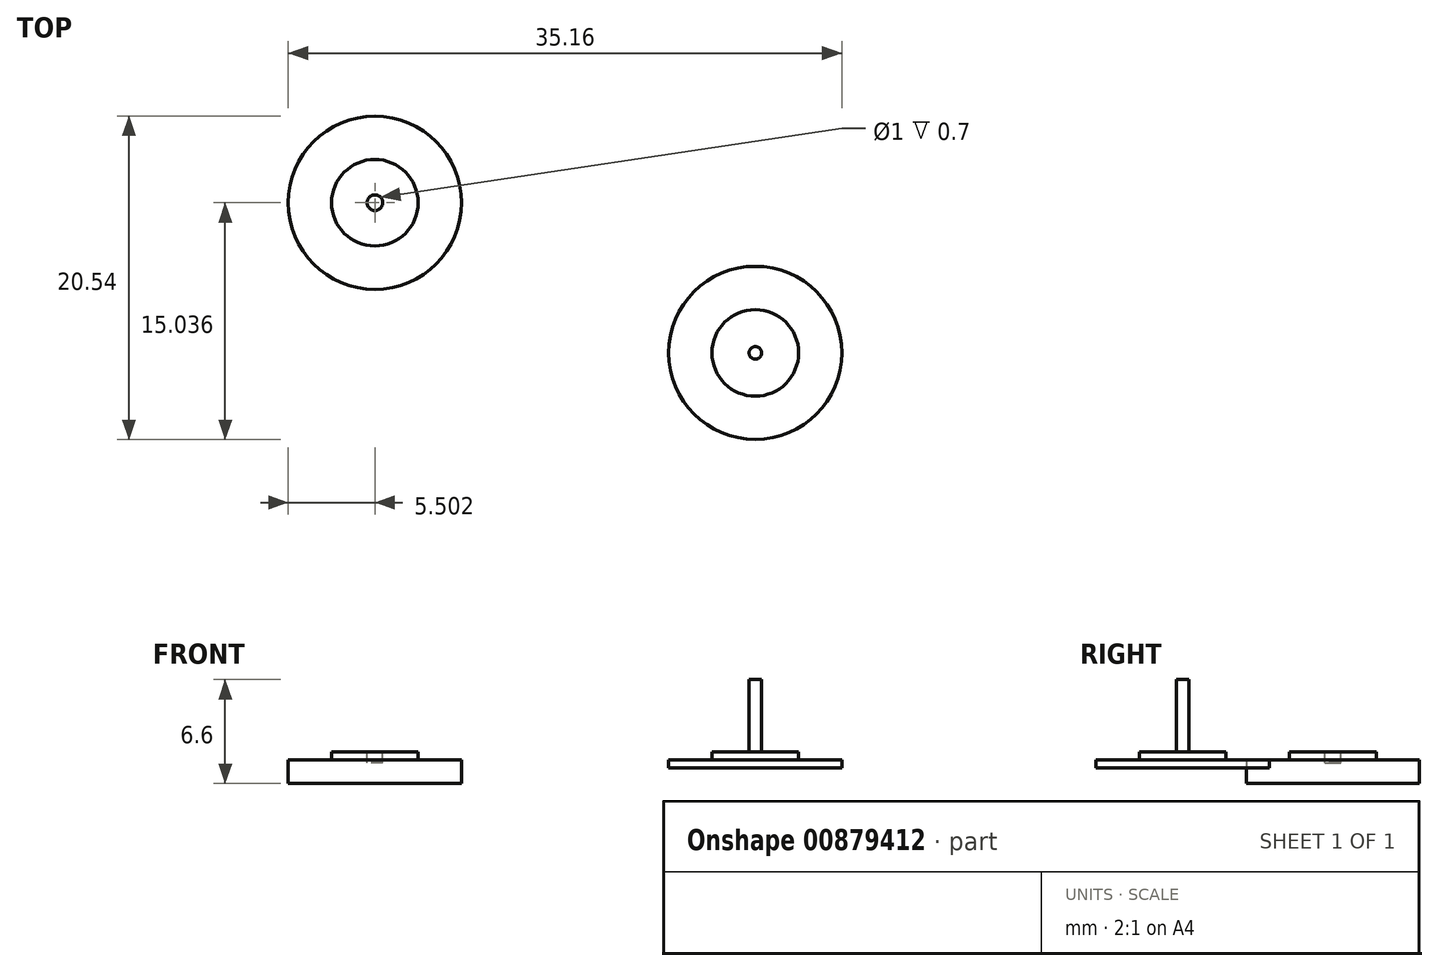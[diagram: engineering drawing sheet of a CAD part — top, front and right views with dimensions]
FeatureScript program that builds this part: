
annotation { "Feature Type Name" : "Feature", "Feature Type Description" : "" }
export const myFeature = defineFeature(function(context is Context, id is Id, definition is map)
    precondition{}
    {
        {
            var Q0;
            Q0=qCreatedBy(makeId("Top.planeOp"),FACE);
            var sketch = newSketch(context, id + "F0", { "sketchPlane" : qUnion([Q0])});
            skCircle(sketch, "E0", {"center": v(-49.28, 41.97) * mm, "radius": 5.5 * mm});
            skSolve(sketch);
        }
        {
            var Q0;
            Q0=makeQuery(id+"F0.imprint","IMPRINT",FACE,{"disambiguationData":[TD([[makeQuery(id+"F0.imprint","IMPRINT",EDGE,{"derivedFrom":sQuery(id+"F0.wireOp",EDGE,"E0")}),1.0]])]});
            extrude(context, id + "F1", {"entities" : qUnion([Q0]), "depth" : .5 * mm, "offsetDistance" : 25.4 * mm});
        }
        {
            var Q0;
            Q0=qCreatedBy(makeId("Top.planeOp"),FACE);
            var sketch = newSketch(context, id + "F2", { "sketchPlane" : qUnion([Q0])});
            skCircle(sketch, "E1", {"center": v(-25.12, 32.43) * mm, "radius": 5.5 * mm});
            skSolve(sketch);
        }
        {
            var Q0;
            Q0=makeQuery(id+"F2.imprint","IMPRINT",FACE,{"disambiguationData":[TD([[makeQuery(id+"F2.imprint","IMPRINT",EDGE,{"derivedFrom":sQuery(id+"F2.wireOp",EDGE,"E1")}),1.0]])]});
            extrude(context, id + "F3", {"entities" : qUnion([Q0]), "depth" : .5 * mm, "offsetDistance" : 25.4 * mm});
        }
        {
            var Q0;
            Q0=qCreatedBy(makeId("Top.planeOp"),FACE);
            var sketch = newSketch(context, id + "F4", { "sketchPlane" : qUnion([Q0])});
            skCircle(sketch, "E2", {"center": v(-49.28, 41.97) * mm, "radius": 2.75 * mm});
            skSolve(sketch);
        }
        {
            var Q0;
            Q0 = qSketchRegion(id + "F4", true);
            extrude(context, id + "F5", {"entities" : qUnion([Q0]), "operationType" : NewBodyOperationType.ADD, "depth" : 1 * mm, "offsetDistance" : 25.4 * mm});
        }
        {
            var Q0;
            Q0=qCreatedBy(makeId("Top.planeOp"),FACE);
            var sketch = newSketch(context, id + "F6", { "sketchPlane" : qUnion([Q0])});
            skCircle(sketch, "E3", {"center": v(-25.12, 32.43) * mm, "radius": 2.75 * mm});
            skSolve(sketch);
        }
        {
            var Q0;
            Q0 = qSketchRegion(id + "F6", true);
            extrude(context, id + "F7", {"entities" : qUnion([Q0]), "operationType" : NewBodyOperationType.ADD, "depth" : 1 * mm, "offsetDistance" : 25.4 * mm});
        }
        {
            var Q0;
            Q0=makeQuery(id+"F5.opExtrude","CAP_FACE",FACE,{"disambiguationData":[OSD([sQuery(id+"F4.wireOp",EDGE,"E2")])],"isStart":false});
            var sketch = newSketch(context, id + "F8", { "sketchPlane" : qUnion([Q0])});
            skCircle(sketch, "E4", {"center": v(-49.28, 41.97) * mm, "radius": 0.5 * mm});
            skSolve(sketch);
        }
        {
            var Q0;
            Q0 = qSketchRegion(id + "F8", true);
            extrude(context, id + "F9", {"entities" : qUnion([Q0]), "operationType" : NewBodyOperationType.REMOVE, "oppositeDirection" : true, "depth" : .7 * mm, "offsetDistance" : 25.4 * mm});
        }
        {
            var Q0;
            Q0=makeQuery(id+"F7.opExtrude","CAP_FACE",FACE,{"disambiguationData":[OSD([sQuery(id+"F6.wireOp",EDGE,"E3")])],"isStart":false});
            var sketch = newSketch(context, id + "F10", { "sketchPlane" : qUnion([Q0])});
            skCircle(sketch, "E5", {"center": v(-25.12, 32.43) * mm, "radius": 0.4 * mm});
            skSolve(sketch);
        }
        {
            var Q0;
            Q0 = qSketchRegion(id + "F10", true);
            extrude(context, id + "F11", {"entities" : qUnion([Q0]), "operationType" : NewBodyOperationType.ADD, "depth" : 4.6 * mm, "offsetDistance" : 25.4 * mm});
        }
        {
            var Q0;
            Q0=sQuery(id+"F2.wireOp",EDGE,"E1");
            extrude(context, id + "F12", {"bodyType" : ToolBodyType.SURFACE, "surfaceEntities" : qUnion([Q0]), "oppositeDirection" : true, "depth" : 1 * mm, "offsetDistance" : 25.4 * mm});
        }
        {
            var Q0;
            Q0=makeQuery(id+"F0.imprint","IMPRINT",FACE,{"disambiguationData":[TD([[makeQuery(id+"F0.imprint","IMPRINT",EDGE,{"derivedFrom":sQuery(id+"F0.wireOp",EDGE,"E0")}),1.0]])]});
            extrude(context, id + "F13", {"entities" : qUnion([Q0]), "operationType" : NewBodyOperationType.ADD, "oppositeDirection" : true, "depth" : 1 * mm, "offsetDistance" : 25.4 * mm});
        }
    });
